# Revit family: Valve-Diverter-Waterworks-Universal-Pressure_Balance
name_source: partatom
category: Pipe Accessories
revit_build: Autodesk Revit MEP 2014 (Build: 20140709_2115(x64)
units: mm (PartAtom-declared; Revit-internal decimal feet)

## types (1)
- Universal Pressure Balance with Diverter Valve
    ADA Compliant = Yes
    Anti-scald Protection = Yes
    Assembly Code = D2010
    Certification CSA = Yes
    Certification IAPMO = Yes
    Certification State of MA = Yes
    Certification UPC = Yes
    Certification cUPC = Yes
    Code Compliance = Code # GUSV87: ASME A112.18.1 / CSA B125.1, IAPMO, CSA, State of MA
    Cold Water Inlet Connection = Inlet - Copper Sweat
    Cold Water Inlet Diameter = 0' - 0 1/2"
    Control Valve Rough-in Depth Maximum = 0' - 2 7/8"
    Control Valve Rough-in Depth Minimum = 0' - 1 7/8"
    Depth = 0' - 5 3/4"
    Description = Universal Pressure Balance with Diverter Valve
    Finish = Metal - Waterworks - Brass
    Fittings Hole Diameter = 0' - 3 1/2"
    Height = 0' - 3 3/4"
    Hot Water Inlet Connection = Inlet - Copper Sweat
    Hot Water Inlet Diameter = 0' - 0 1/2"
    Keynote = 22 40 00
    Length = 0' - 4 3/4"
    Manufacturer = Waterworks
    Mixed Water Bottom Outlet Diameter = 0' - 0 1/2"
    Mixed Water Outlet Bottom Connection = Oulet - Sweat Shower/ NPT Tub
    Mixed Water Outlet Top Connection = Oulet - Sweat Shower/ NPT Tub
    Mixed Water Top Outlet Diamter = 0' - 0 1/2"
    Model = GUPB87
    Model SKU = 26-29053-55752
    Pressure = 45.00 psi
    Product Documentation Link = http://assets.waterworks.com
    Product Name = Universal Pressure Balance with Diverter Valve
    Product Page URL = http://www.waterworks.com
    URL = http://www.waterworks.com
    Version = 2014 - v1.0a
    Warranty = http://www.waterworks.com
    Water Pressure = Max: 85psi / Min: 20psi / Recommended: 45psi
    ‌Installation Requirements or Notes = It is recommended not to exceed 4.2 gpm total,per shower installation; restricted maximum flow rate is controlled by end fitting, see fitting specs for details

## geometry (parser evidence)
native form markers: Sweep x1
no freeform markers — native parametric forms only
